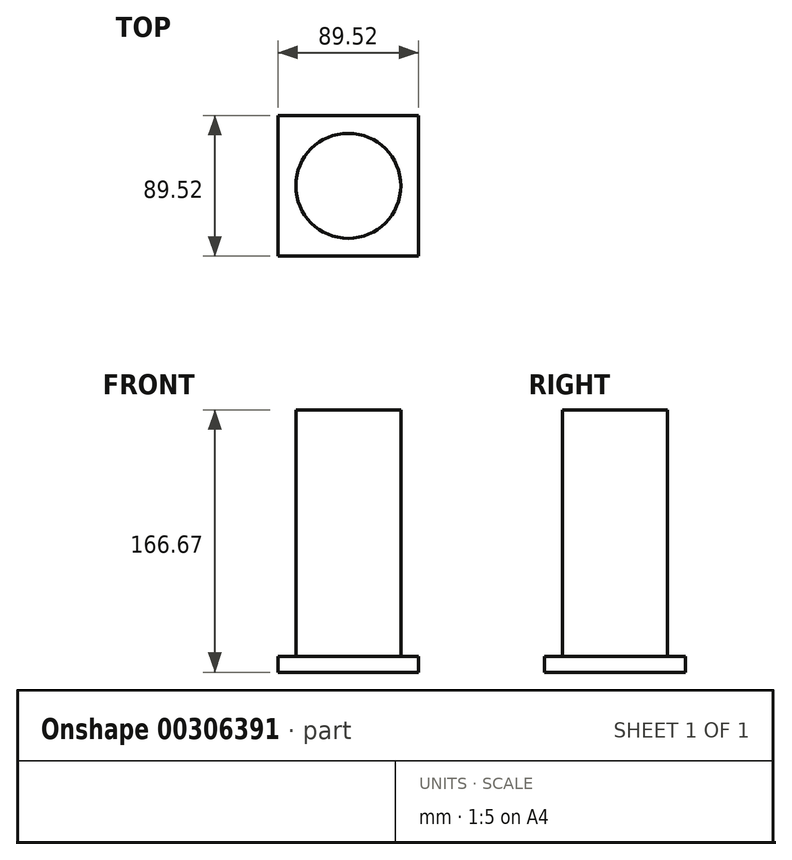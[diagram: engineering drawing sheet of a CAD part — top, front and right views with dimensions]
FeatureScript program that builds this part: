
annotation { "Feature Type Name" : "Feature", "Feature Type Description" : "" }
export const myFeature = defineFeature(function(context is Context, id is Id, definition is map)
    precondition{}
    {
        {
            var Q0;
            Q0=qCreatedBy(makeId("Front.planeOp"),FACE);
            var sketch = newSketch(context, id + "F0", { "sketchPlane" : qUnion([Q0])});
            skLineSegment(sketch, "E0.bottom", {"start": v(0, 166.67) * mm, "end": v(33.33, 166.67) * mm});
            skLineSegment(sketch, "E0.top", {"start": v(0, 0) * mm, "end": v(33.33, 0) * mm});
            skLineSegment(sketch, "E0.left", {"start": v(0, 166.67) * mm, "end": v(0, 0) * mm});
            skLineSegment(sketch, "E0.right", {"start": v(33.33, 166.67) * mm, "end": v(33.33, 0) * mm});
            skSolve(sketch);
        }
        {
            var Q0;
            Q0 = qSketchRegion(id + "F0", true);
            var Q1;
            Q1=sQuery(id+"F0.wireOp",EDGE,"E0.left");
            revolve(context, id + "F1", {"entities" : qUnion([Q0]), "axis" : qUnion([Q1]), "revolveType" : RevolveType.FULL});
        }
        {
            var Q0;
            Q0=qCreatedBy(makeId("Top.planeOp"),FACE);
            var sketch = newSketch(context, id + "F2", { "sketchPlane" : qUnion([Q0])});
            skLineSegment(sketch, "E1.bottom", {"start": v(-44.76, -44.76) * mm, "end": v(44.76, -44.76) * mm});
            skLineSegment(sketch, "E1.top", {"start": v(-44.76, 44.76) * mm, "end": v(44.76, 44.76) * mm});
            skLineSegment(sketch, "E1.left", {"start": v(-44.76, -44.76) * mm, "end": v(-44.76, 44.76) * mm});
            skLineSegment(sketch, "E1.right", {"start": v(44.76, -44.76) * mm, "end": v(44.76, 44.76) * mm});
            skPoint(sketch, "E1.middle", {"position": v(0, 0) * mm});
            skSolve(sketch);
        }
        {
            var Q0;
            Q0=makeQuery(id+"F2.imprint","IMPRINT",FACE,{"disambiguationData":[TD([[makeQuery(id+"F2.imprint","IMPRINT",EDGE,{"derivedFrom":sQuery(id+"F2.wireOp",EDGE,"E1.bottom")}),1.0]])]});
            extrude(context, id + "F3", {"entities" : qUnion([Q0]), "operationType" : NewBodyOperationType.ADD, "depth" : 10 * mm});
        }
    });
